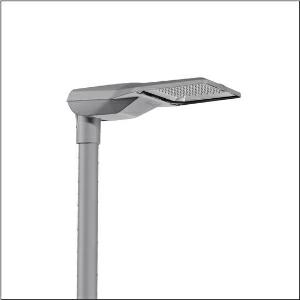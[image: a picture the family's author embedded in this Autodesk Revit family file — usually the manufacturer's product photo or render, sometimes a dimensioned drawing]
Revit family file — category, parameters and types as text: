
# Revit family: streetlight_sl_21_iq_midi___st1_0a_5xe3d21d08nb_d513
name_source: partatom
category: Lighting Fixtures
units: mm (PartAtom-declared; Revit-internal decimal feet)

## family parameters
Cut with Voids When Loaded = No
Host = Face
Light Source = No
Part Type = Normal
Room Calculation Point = No
Round Connector Dimension = Use Diameter
Shared = No

## types (1)
- --- (1 x LED, 19210 lm, 155.5 W, 2200K)
    Apparent Load = 155 VA
    CIE Flux Codes = 40 73 97 100 100
    Color Rendering = 70
    Color Temperature = 2200K
    Default Elevation = 1800 mm
    Description = Streetlight SL 21 iQ midi, mast luminaire, primary light control with lens, of PMMA, primary optical cover: cover, of toughened safety glass, transparent, light distribution: ST1.0a, light emission: direct distribution, primary light characteristic: asymmetric, installation type: post-top, side-entry, LED, High Power LED, rated luminous flux: 19.210lm, luminous efficacy: 124lm/W, light colour: 722, colour temperature: 2200K, control: Auto-Match, Temp-Guard, Lumen-Switch, Night-Set, Smart-Wire, Light-Fading, Desk-Remote (wireless, voltage-free reading and setting of iQ features in the workshop via application-optimized NFC function/RFID function), optimised constant luminous flux control (CLO 2.0), presetting dimming linear, mains connection: 230..240V, AC, 50/60Hz, start of lifetime: 156W, end of service life: 162W, reduction: 69W, luminaire housing, of diecast aluminium, powder-coated, Siteco® metallic grey (DB 702S), corrosivity category C5 mid according to DIN EN ISO 12944, please order mast flange separately, inclination adjustable: 0°, 5°, 10°, 15°, sealing non-destructively replaceable, multi-level sealing system, length: 644mm, width: 335mm, height: 110mm, mast flange for spigot size: 42mm (side-entry): 5XC10008XM4, 60/48mm (side-entry/post-top): 5XC10108XM2, 76/60mm (side-entry/post-top): 5XC10108XM1, protection rating (complete): IP66, insulation class (complete): insulation class II (safety insulation), certification: CE, ENEC, ENEC+, VDE, impact resistance: IK09, permissible operating ambient temperature for outdoor applications: -40..+50°C, standard-compliant lighting for roads and squares, packaging unit: 1 piece

Light Distribution: ST1.0a
    Height = 111 mm
    Lamp = 1 x LED
    Lamp Light Flux = 19210 lm
    Lamp Power = 155.5 W
    Lamp count = 1
    Length = 644 mm
    Luminous efficacy = 124 lm/W
    Manufacturer = Siteco
    ModVariant = No
    Model = 5XE3D21D08NB
    Number of Poles = 1
    OnlyDefault = Yes
    Power Factor = 1
    Product Name = Streetlight SL 21 iQ midi | ST1.0a
    Product group = mast luminaire | pylon top
    ProductGroupID = 6100
    Protection Class = Protection class II
    Protection Degree = IP 66
    RLX_Detail_Level = 1
    RLX_Emergency_Light_Flux = 0 lm
    RLX_Emergency_Type = 0
    RLX_Emergency_Type_DB = No
    RlxData = <blob elided: 90817 chars, md5=9cfbc46e>
    Socket = socket
    Standby Power = 0 W
    System Light Flux = 19210 lm
    System Power = 155 W
    Type Comments = factory setting: luminous flux: 100 % | dim-lin: 254 | 823 mA
    Type Image = l_1004298.jpg
    URL = http://relux.com
    VarID = @adj_103703
    Voltage = 0 V
    Weight = 0.00 kg
    Width = 336 mm

## geometry (parser evidence)
native form markers: Blend x4, Sweep x10
no freeform markers — native parametric forms only
